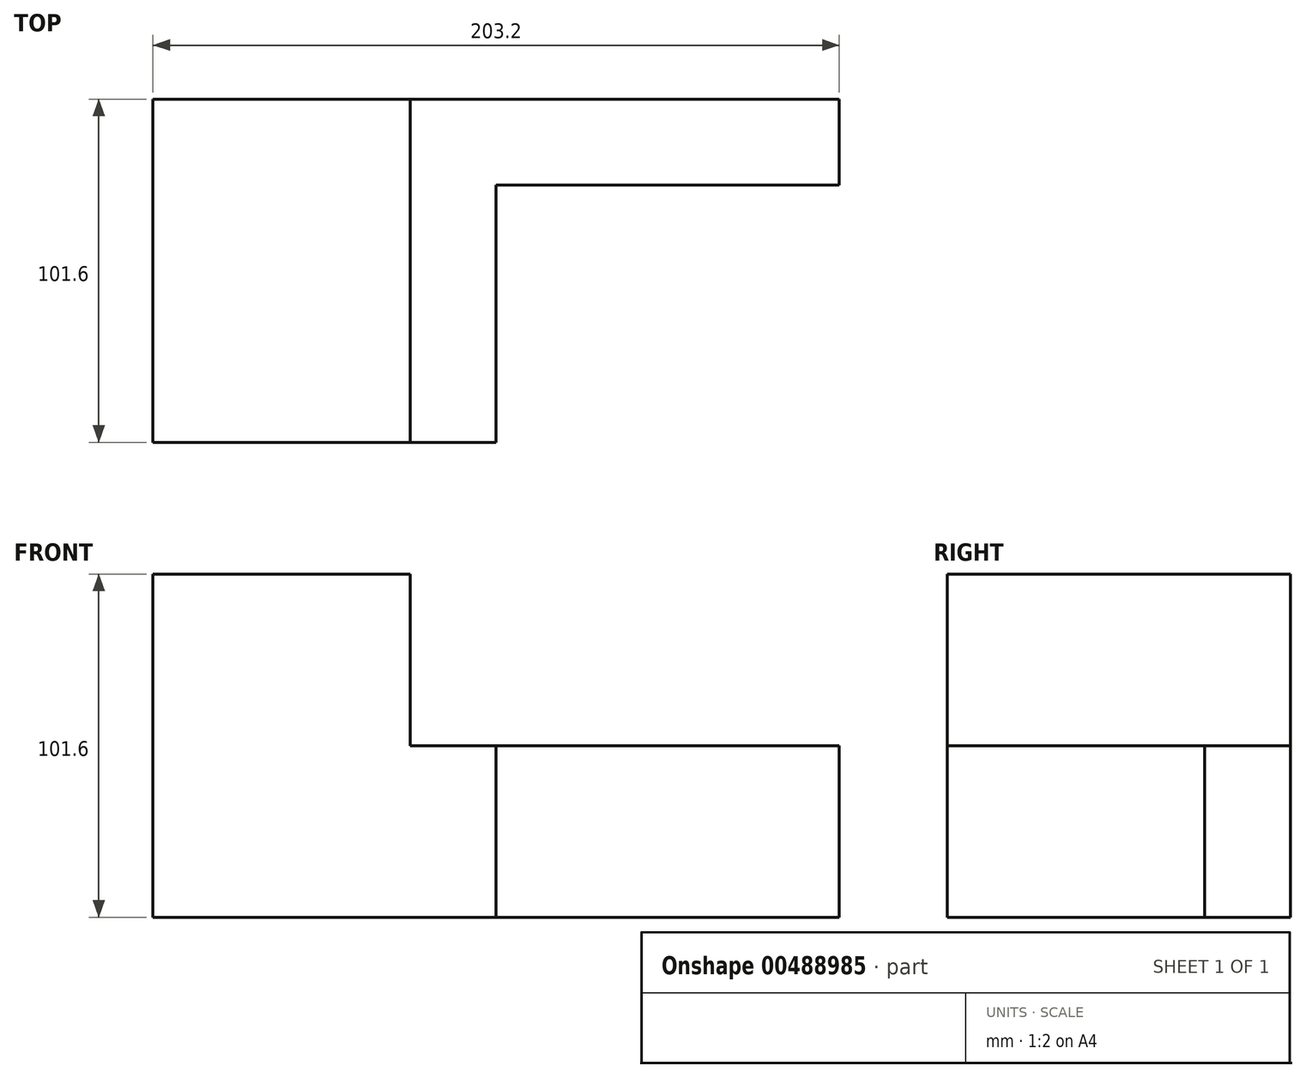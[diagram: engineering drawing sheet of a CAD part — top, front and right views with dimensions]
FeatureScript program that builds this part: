
annotation { "Feature Type Name" : "Feature", "Feature Type Description" : "" }
export const myFeature = defineFeature(function(context is Context, id is Id, definition is map)
    precondition{}
    {
        {
            var Q0;
            Q0=qCreatedBy(makeId("Front.planeOp"),FACE);
            var sketch = newSketch(context, id + "F0", { "sketchPlane" : qUnion([Q0])});
            skLineSegment(sketch, "E0.bottom", {"start": v(-63.82, 23.12) * mm, "end": v(139.38, 23.12) * mm});
            skLineSegment(sketch, "E0.top", {"start": v(-63.82, -27.68) * mm, "end": v(139.38, -27.68) * mm});
            skLineSegment(sketch, "E0.left", {"start": v(-63.82, 23.12) * mm, "end": v(-63.82, -27.68) * mm});
            skLineSegment(sketch, "E0.right", {"start": v(139.38, 23.12) * mm, "end": v(139.38, -27.68) * mm});
            skLineSegment(sketch, "E1.bottom", {"start": v(-63.82, 23.12) * mm, "end": v(12.38, 23.12) * mm});
            skLineSegment(sketch, "E1.top", {"start": v(-63.82, 73.92) * mm, "end": v(12.38, 73.92) * mm});
            skLineSegment(sketch, "E1.left", {"start": v(-63.82, 23.12) * mm, "end": v(-63.82, 73.92) * mm});
            skLineSegment(sketch, "E1.right", {"start": v(12.38, 23.12) * mm, "end": v(12.38, 73.92) * mm});
            skSolve(sketch);
        }
        {
            var Q0;
            Q0=qSketchRegion(id+"F0",true);
            extrude(context, id + "F1", {"entities" : qUnion([Q0]), "depth" : 101.6 * mm});
        }
        {
            var Q0;
            Q0=makeQuery(id+"F1.opExtrude","SWEPT_FACE",FACE,{"disambiguationData":[OSD([sQuery(id+"F0.wireOp",EDGE,"E0.bottom")])]});
            var sketch = newSketch(context, id + "F2", { "sketchPlane" : qUnion([Q0])});
            skLineSegment(sketch, "E2.bottom", {"start": v(139.38, -101.6) * mm, "end": v(37.78, -101.6) * mm});
            skLineSegment(sketch, "E2.top", {"start": v(139.38, -25.4) * mm, "end": v(37.78, -25.4) * mm});
            skLineSegment(sketch, "E2.left", {"start": v(139.38, -101.6) * mm, "end": v(139.38, -25.4) * mm});
            skLineSegment(sketch, "E2.right", {"start": v(37.78, -101.6) * mm, "end": v(37.78, -25.4) * mm});
            skSolve(sketch);
        }
        {
            var Q0;
            Q0 = qSketchRegion(id + "F2", true);
            extrude(context, id + "F3", {"entities" : qUnion([Q0]), "operationType" : NewBodyOperationType.REMOVE, "endBound" : BoundingType.THROUGH_ALL, "oppositeDirection" : true, "depth" : 25.4 * mm});
        }
    });
